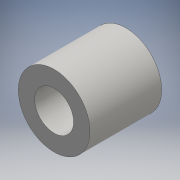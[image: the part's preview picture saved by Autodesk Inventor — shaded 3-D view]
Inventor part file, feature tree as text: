
AUTODESK INVENTOR PART (.ipt)
format: ipt  version: 2016 (Build 200138000, 138)  size: 97,280 bytes
history: native  units: mm
features: extrude x2, sketch x2, other x1
ambient origin geometry x8: Origin, YZ Plane, XZ Plane, XY Plane, X Axis, Y Axis, Z Axis, Center Point
bodies: Body1 (feature_tree)
feature tree (5):
  other  "ソリッド1"
  extrude  "押し出し1"  Depth=35.0mm
  extrude  "押し出し2"  Depth=35.0mm TaperAngle=0.0deg
  sketch  "スケッチ1"
  sketch  "スケッチ2"
